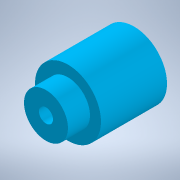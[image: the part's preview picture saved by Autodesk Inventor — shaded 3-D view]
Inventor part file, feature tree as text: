
AUTODESK INVENTOR PART (.ipt)
format: ipt  version: 2020 (Build 240168000, 168)  size: 140,288 bytes
history: native  units: mm
features: extrude x2, sketch x2, other x1, projected_geometry x1
ambient origin geometry x8: Origin, YZ Plane, XZ Plane, XY Plane, X Axis, Y Axis, Z Axis, Center Point
bodies: Body1 (feature_tree)
feature tree (6):
  other  "ソリッド1"
  extrude  "押し出し1"  Depth=12.0mm
  extrude  "押し出し2"  Depth=15.0mm TaperAngle=0.0deg
  sketch  "スケッチ1"
  sketch  "スケッチ2"
  projected_geometry  "投影ループ1"
